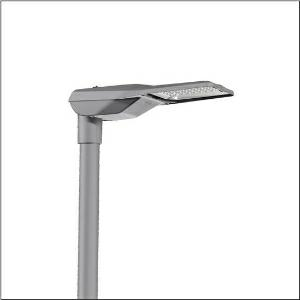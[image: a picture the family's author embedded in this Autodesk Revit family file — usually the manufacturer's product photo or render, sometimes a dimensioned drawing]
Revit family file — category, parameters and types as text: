
# Revit family: streetlight_sl_21_mini___st1_0a_5xe2d43s08hb_695f
name_source: partatom
category: Lighting Fixtures
units: mm (PartAtom-declared; Revit-internal decimal feet)

## family parameters
Cut with Voids When Loaded = No
Host = Face
Light Source = No
Part Type = Normal
Room Calculation Point = No
Round Connector Dimension = Use Diameter
Shared = No

## types (1)
- --- (1 x LED, 9430 lm, 66 W, 4000K)
    Apparent Load = 66 VA
    CIE Flux Codes = 37 72 97 100 100
    Color Rendering = 70
    Color Temperature = 4000K
    Default Elevation = 1800 mm
    Description = Streetlight SL 21 mini, mast luminaire, primary light control with lens, of PMMA, primary optical cover: cover, of toughened safety glass, transparent, light distribution: ST1.0a, light emission: direct distribution, primary light characteristic: asymmetric, installation type: side-entry, post-top, LED, High Power LED, rated luminous flux: 9.430lm, luminous efficacy: 143lm/W, light colour: 740, colour temperature: 4000K, control gear: D4i, control: overheat protection, constant luminous flux control, time-dependent luminous flux control, flexible luminous flux parameterisation, pre-setting: logarithmic dimming characteristic, mains connection: 220..240V, AC, 50/60Hz, start of lifetime: 66W, end of service life: 69W, reduction: 30W, luminaire housing, of diecast aluminium, powder-coated, SITECO metallic grey (DB 702S), corrosivity category C5 high according to DIN EN ISO 12944, please order mast flange separately, inclination adjustable: 0°, 5°, 10°, 15°, sealing non-destructively replaceable, multi-level sealing system, length: 628mm, width: 235mm, height: 110mm, mast flange for spigot size: 42mm (side-entry): 5XC10008XM4, 60/48mm (side-entry/post-top): 5XC10108XM2, 76/60mm (side-entry/post-top): 5XC10108XM1, mounting height: 4..8m, Smart Interface above, protection rating (complete): IP66, insulation class (complete): insulation class II (safety insulation), certification: CE, ENEC, ENEC+, VDE, impact resistance: IK10, permissible operating ambient temperature for outdoor applications: -40..+50°C, standard-compliant lighting for roads and squares, packaging unit: 1 piece

Light Distribution: ST1.0a
    Height = 110 mm
    Lamp = 1 x LED
    Lamp Light Flux = 9430 lm
    Lamp Power = 66 W
    Lamp count = 1
    Length = 625 mm
    Luminous efficacy = 143 lm/W
    Manufacturer = Siteco
    ModVariant = No
    Model = 5XE2D43S08HB
    Number of Poles = 1
    OnlyDefault = Yes
    Power Factor = 1
    Product Name = Streetlight SL 21 mini | ST1.0a
    Product group = mast luminaire | pylon top
    ProductGroupID = 6100
    Protection Class = Protection class II
    Protection Degree = IP 66
    RLX_Detail_Level = 1
    RLX_Emergency_Light_Flux = 0 lm
    RLX_Emergency_Type = 0
    RLX_Emergency_Type_DB = No
    RlxData = <blob elided: 26133 chars, md5=57a0273c>
    Socket = socket
    Standby Power = 0 W
    System Light Flux = 9430 lm
    System Power = 66 W
    Type Comments = factory setting: luminous flux: 100 % | dim-lin: 254 | 670 mA
    Type Image = l_1003515.jpg
    URL = http://relux.com
    VarID = @adj_186083
    Voltage = 0 V
    Weight = 0.00 kg
    Width = 234 mm

## geometry (parser evidence)
native form markers: Blend x4, Sweep x12
no freeform markers — native parametric forms only
